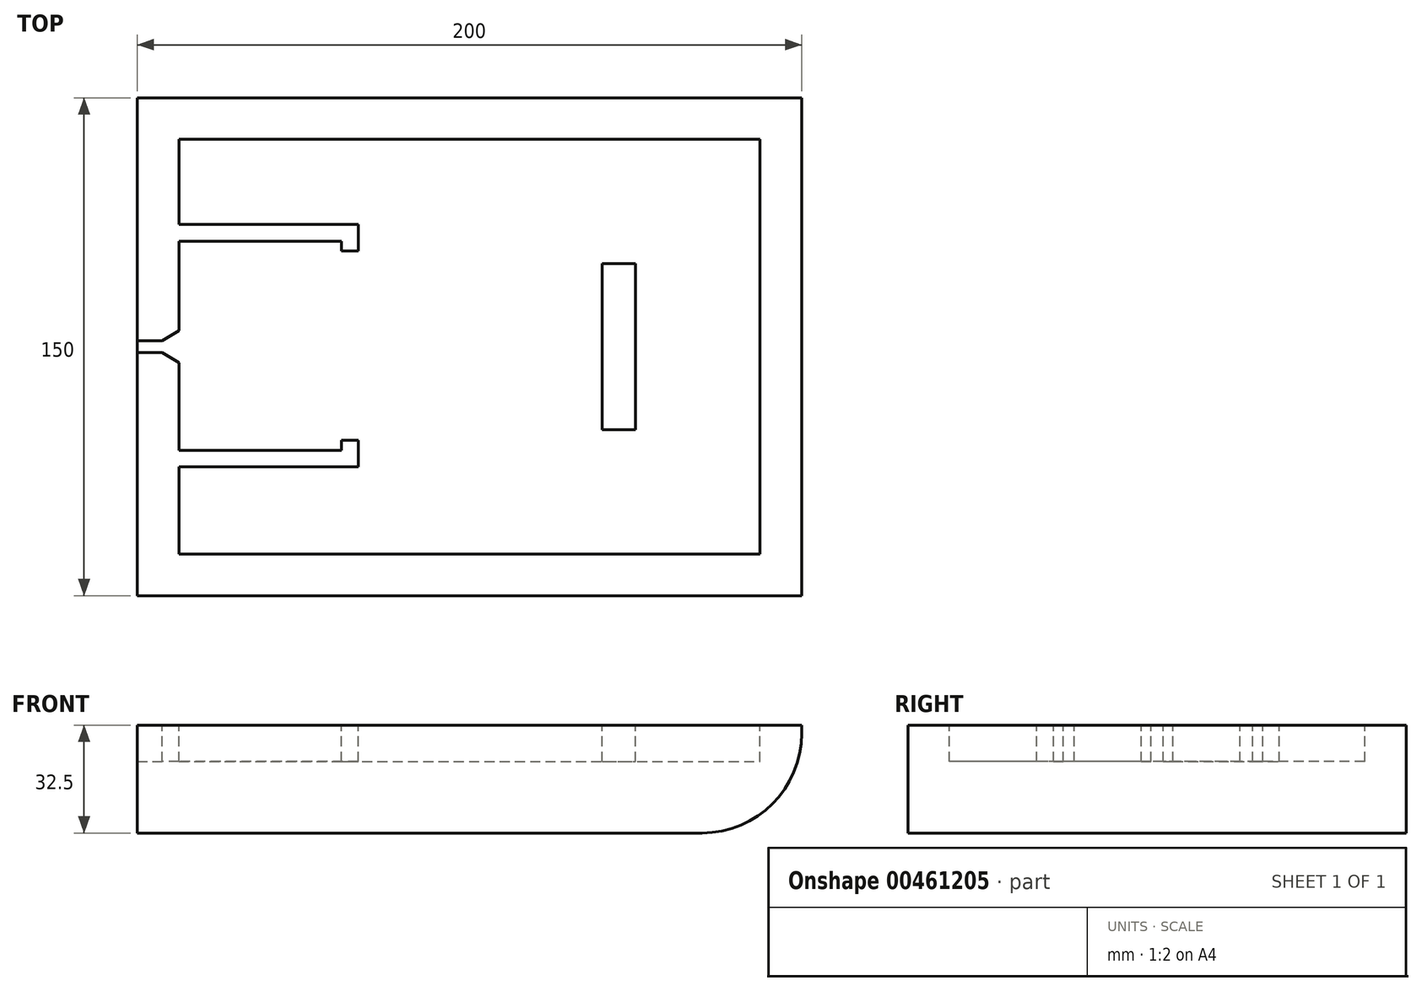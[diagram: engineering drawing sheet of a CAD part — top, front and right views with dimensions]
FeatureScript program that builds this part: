
annotation { "Feature Type Name" : "Feature", "Feature Type Description" : "" }
export const myFeature = defineFeature(function(context is Context, id is Id, definition is map)
    precondition{}
    {
        {
            var Q0;
            Q0=qCreatedBy(makeId("Front.planeOp"),FACE);
            var sketch = newSketch(context, id + "F0", { "sketchPlane" : qUnion([Q0])});
            skLineSegment(sketch, "E0.bottom", {"start": v(100, 16.25) * mm, "end": v(-100, 16.25) * mm});
            skLineSegment(sketch, "E0.top", {"start": v(70, -16.25) * mm, "end": v(-100, -16.25) * mm});
            skLineSegment(sketch, "E0.left", {"start": v(100, 16.25) * mm, "end": v(100, 13.75) * mm});
            skLineSegment(sketch, "E0.right", {"start": v(-100, 16.25) * mm, "end": v(-100, -16.25) * mm});
            skPoint(sketch, "E0.middle", {"position": v(0, 0) * mm});
            skPoint(sketch, "E1.visualSharp", {"position": v(100, -16.25) * mm});
            skArc(sketch, "E1.filletArc", {"start": v(70, -16.25) * mm, "mid": v(91.21, -7.46) * mm, "end": v(100, 13.75) * mm});
            skSolve(sketch);
        }
        {
            var Q0;
            Q0=qSketchRegion(id+"F0",true);
            extrude(context, id + "F1", {"entities" : qUnion([Q0]), "endBound" : BoundingType.SYMMETRIC, "oppositeDirection" : true, "depth" : 150 * mm});
        }
        {
            var Q0;
            Q0=makeQuery(id+"F1.opExtrude","SWEPT_FACE",FACE,{"disambiguationData":[OSD([sQuery(id+"F0.wireOp",EDGE,"E0.bottom")])]});
            var sketch = newSketch(context, id + "F2", { "sketchPlane" : qUnion([Q0])});
            skLineSegment(sketch, "E2.bottom", {"start": v(87.5, 62.5) * mm, "end": v(-87.5, 62.5) * mm});
            skLineSegment(sketch, "E2.top", {"start": v(87.5, -62.5) * mm, "end": v(-77.5, -62.5) * mm});
            skLineSegment(sketch, "E2.left", {"start": v(87.5, 62.5) * mm, "end": v(87.5, -62.5) * mm});
            skLineSegment(sketch, "E2.right", {"start": v(-87.5, 62.5) * mm, "end": v(-87.5, 36.79) * mm});
            skPoint(sketch, "E2.middle", {"position": v(0, 0) * mm});
            skLineSegment(sketch, "E3.bottom", {"start": v(-87.5, 31.79) * mm, "end": v(-46, 31.79) * mm});
            skLineSegment(sketch, "E4", {"start": v(-46, -36.21) * mm, "end": v(-87.5, -36.21) * mm});
            skLineSegment(sketch, "E5", {"start": v(-41, -36.21) * mm, "end": v(-46, -36.21) * mm});
            skLineSegment(sketch, "E6", {"start": v(-41, 36.79) * mm, "end": v(-87.5, 36.79) * mm});
            skLineSegment(sketch, "E7.trimOffspring", {"start": v(-87.5, -36.21) * mm, "end": v(-87.5, -62.5) * mm});
            skLineSegment(sketch, "E8", {"start": v(-6, -28.21) * mm, "end": v(-6, 28.79) * mm});
            skLineSegment(sketch, "E9", {"start": v(-74.36, 52.5) * mm, "end": v(60.64, 52.5) * mm});
            skLineSegment(sketch, "E10", {"start": v(60.64, 49.5) * mm, "end": v(-74.36, 49.5) * mm});
            skLineSegment(sketch, "E11", {"start": v(-74.36, 52.5) * mm, "end": v(-77.36, 52.5) * mm});
            skLineSegment(sketch, "E12", {"start": v(-77.36, 52.5) * mm, "end": v(-77.36, 49.5) * mm});
            skLineSegment(sketch, "E13", {"start": v(-77.36, 49.5) * mm, "end": v(-74.36, 49.5) * mm});
            skLineSegment(sketch, "E14", {"start": v(-87.5, -62.5) * mm, "end": v(-77.5, -62.5) * mm});
            skLineSegment(sketch, "E15", {"start": v(-77.5, -52.5) * mm, "end": v(60.64, -52.5) * mm});
            skLineSegment(sketch, "E16", {"start": v(60.64, -49.5) * mm, "end": v(-77.5, -49.5) * mm});
            skLineSegment(sketch, "E17", {"start": v(-77.5, -52.5) * mm, "end": v(-77.5, -49.5) * mm});
            skLineSegment(sketch, "E18", {"start": v(60.64, 49.5) * mm, "end": v(57.64, 49.5) * mm});
            skLineSegment(sketch, "E19", {"start": v(60.64, 52.5) * mm, "end": v(77.5, 52.5) * mm});
            skLineSegment(sketch, "E20", {"start": v(77.5, 52.5) * mm, "end": v(77.5, -52.5) * mm});
            skLineSegment(sketch, "E21", {"start": v(77.5, -52.5) * mm, "end": v(60.64, -52.5) * mm});
            skLineSegment(sketch, "E22", {"start": v(77.5, 52.5) * mm, "end": v(77.5, 49.5) * mm});
            skLineSegment(sketch, "E23", {"start": v(69.5, 49.5) * mm, "end": v(60.64, 49.5) * mm});
            skLineSegment(sketch, "E24", {"start": v(77.5, 52.5) * mm, "end": v(74.5, 52.5) * mm});
            skLineSegment(sketch, "E25", {"start": v(74.5, 44.5) * mm, "end": v(74.5, -44.5) * mm});
            skLineSegment(sketch, "E26", {"start": v(60.64, -49.5) * mm, "end": v(69.5, -49.5) * mm});
            skPoint(sketch, "E27.end.orphan", {"position": v(77.5, 50.73) * mm});
            skArc(sketch, "E28.filletArc", {"start": v(74.5, 44.5) * mm, "mid": v(73.04, 48.04) * mm, "end": v(69.5, 49.5) * mm});
            skPoint(sketch, "E29.visualSharp", {"position": v(74.5, -49.5) * mm});
            skArc(sketch, "E29.filletArc", {"start": v(69.5, -49.5) * mm, "mid": v(73.04, -48.04) * mm, "end": v(74.5, -44.5) * mm});
            skLineSegment(sketch, "E30", {"start": v(-87.5, 31.79) * mm, "end": v(-38.5, 31.79) * mm});
            skLineSegment(sketch, "E31", {"start": v(-38.5, 31.79) * mm, "end": v(-38.5, 28.79) * mm});
            skLineSegment(sketch, "E32", {"start": v(-38.5, 28.79) * mm, "end": v(-33.5, 28.79) * mm});
            skLineSegment(sketch, "E33", {"start": v(-33.5, 28.79) * mm, "end": v(-33.5, 36.79) * mm});
            skLineSegment(sketch, "E34", {"start": v(-33.5, 36.79) * mm, "end": v(-41, 36.79) * mm});
            skLineSegment(sketch, "E35", {"start": v(-100, 1.8) * mm, "end": v(-100, -1.8) * mm});
            skLineSegment(sketch, "E36", {"start": v(-100, 1.8) * mm, "end": v(-92.5, 1.8) * mm});
            skLineSegment(sketch, "E37", {"start": v(-100, -1.8) * mm, "end": v(-92.5, -1.8) * mm});
            skLineSegment(sketch, "E38", {"start": v(-87.5, -4.8) * mm, "end": v(-92.5, -1.8) * mm});
            skLineSegment(sketch, "E39", {"start": v(-92.5, 1.8) * mm, "end": v(-87.5, 4.8) * mm});
            skLineSegment(sketch, "E40", {"start": v(-87.5, 4.8) * mm, "end": v(-87.5, 31.79) * mm});
            skLineSegment(sketch, "E41", {"start": v(-87.5, -4.8) * mm, "end": v(-87.5, -31.21) * mm});
            skLineSegment(sketch, "E42", {"start": v(-87.5, -31.21) * mm, "end": v(-38.5, -31.21) * mm});
            skLineSegment(sketch, "E43", {"start": v(-38.5, -31.21) * mm, "end": v(-38.5, -28.21) * mm});
            skLineSegment(sketch, "E44", {"start": v(-38.5, -28.21) * mm, "end": v(-33.5, -28.21) * mm});
            skLineSegment(sketch, "E45", {"start": v(-33.5, -28.21) * mm, "end": v(-33.5, -36.21) * mm});
            skLineSegment(sketch, "E46", {"start": v(-33.5, -36.21) * mm, "end": v(-41, -36.21) * mm});
            skPoint(sketch, "E47.start.orphan", {"position": v(-41, -28.21) * mm});
            skLineSegment(sketch, "E48", {"start": v(0, 0) * mm, "end": v(40, 0) * mm});
            skLineSegment(sketch, "E49", {"start": v(40, 0) * mm, "end": v(40, 37.5) * mm});
            skLineSegment(sketch, "E50", {"start": v(40, 0) * mm, "end": v(40, -37.5) * mm});
            skPoint(sketch, "E51.end.orphan", {"position": v(42.98, -37.5) * mm});
            skLineSegment(sketch, "E52", {"start": v(40, 37.5) * mm, "end": v(50, 37.5) * mm});
            skLineSegment(sketch, "E53", {"start": v(50, 37.5) * mm, "end": v(50, -37.5) * mm});
            skLineSegment(sketch, "E54", {"start": v(50, -37.5) * mm, "end": v(40, -37.5) * mm});
            skLineSegment(sketch, "E55", {"start": v(40, 0) * mm, "end": v(40, 25) * mm});
            skLineSegment(sketch, "E56", {"start": v(40, 25) * mm, "end": v(50, 25) * mm});
            skLineSegment(sketch, "E57", {"start": v(40, 0) * mm, "end": v(40, -25) * mm});
            skLineSegment(sketch, "E58", {"start": v(40, -25) * mm, "end": v(50, -25) * mm});
            skSolve(sketch);
        }
        {
            var Q0;
            Q0=makeQuery(id+"F2.imprint","IMPRINT",FACE,{"disambiguationData":[TD([[makeQuery(id+"F2.imprint","IMPRINT",EDGE,{"derivedFrom":sQuery(id+"F2.wireOp",EDGE,"E2.bottom")}),1.0]])]});
            var Q1;
            Q1=makeQuery(id+"F2.imprint","IMPRINT",FACE,{"disambiguationData":[TD([[makeQuery(id+"F2.imprint","IMPRINT",EDGE,{"derivedFrom":sQuery(id+"F2.wireOp",EDGE,"E49")}),-1.0]])]});
            var Q2;
            Q2=makeQuery(id+"F2.imprint","IMPRINT",FACE,{"disambiguationData":[TD([[makeQuery(id+"F2.imprint","IMPRINT",EDGE,{"derivedFrom":sQuery(id+"F2.wireOp",EDGE,"E50")}),1.0]])]});
            var Q3;
            Q3=makeQuery(id+"F2.imprint","IMPRINT",FACE,{"disambiguationData":[TD([[makeQuery(id+"F2.imprint","IMPRINT",EDGE,{"derivedFrom":sQuery(id+"F2.wireOp",EDGE,"E55")}),-1.0]])]});
            var Q4;
            Q4=makeQuery(id+"F2.imprint","IMPRINT",FACE,{"disambiguationData":[TD([[makeQuery(id+"F2.imprint","IMPRINT",EDGE,{"derivedFrom":sQuery(id+"F2.wireOp",EDGE,"E9")}),-1.0]])]});
            extrude(context, id + "F3", {"entities" : qUnion([Q0, Q1, Q2, Q3, Q4]), "operationType" : NewBodyOperationType.REMOVE, "oppositeDirection" : true, "depth" : 11 * mm, "offsetDistance" : 25 * mm});
        }
    });
